# Revit family: Hager-WITTY PRO WALL MOUNTED-fr-FR-FR
name_source: partatom
category: Electrical Fixtures
units: mm (PartAtom-declared; Revit-internal decimal feet)

## family parameters
Always vertical = Yes
Cut with Voids When Loaded = No
Host = Wall
Maintain Annotation Orientation = No
OmniClass Number = 23.75.00.00
OmniClass Title = Climate Control (HVAC)
Part Type = Normal
Room Calculation Point = No
Round Connector Dimension = Use Diameter
Shared = No

## types (1)
- WITTY PRO-1x22kW-3P-XVL122SLM-WALL MOUNTED
    BC_METADATA = {"ObjectGuid":"b7395028-ef9e-46b8-b49f-e0fe9c8fa070","ModelGuid":"b1efb829-c177-4a88-8b0d-f632edc25d22","VariantGuid":"c7b0c534-fef0-4725-a2d6-e8a658ebdb92","Revision":"#2","VariantName":"REF 1"}
    BC_MODEL_ID = 1528908
    BC_OBJECT_ID = 511157
    BC_OBJECT_VERSION = #1
    BC_VARIANT_ID = 1164665
    Code hager = ADD_EC002883_ECVS_WO
    Default Elevation = 0 mm  [stored 0 ft]
    EF000003 - mode de pose = montage mural
    EF000008 - largeur = 250 mm  [stored 0.82021 ft]
    EF000040 - hauteur = 370 mm  [stored 1.21391 ft]
    EF000049 - profondeur = 150 mm  [stored 0.492126 ft]
    EF000458 - avec affichage = No
    EF001596 - matériau du boîtier/corps = plastique
    EF002136 - puissance de raccordement nominale = 22000 W
    EF003840 - tension d'entrée = 400 V
    EF004293 - indice de protection contre les chocs (IK) = IK10
    EF005455 - fréquence = 50/60 Hz
    EF005474 - indice de protection (IP) = IP55
    EF006577 - nombre de prises CEE = 0
    EF007001 - tension de sortie CC = 0 V
    EF007353 - courant de sortie max. CC = 0 A
    EF008200 - section de conducteur connectable = 0 m²
    EF009078 - nombre de points de chargement = 1
    EF009089 - avec boîte de raccordement domestique = No
    EF009091 - nombre d'interrupteurs différentiels type A = 0
    EF009092 - nombre d'interrupteurs différentiels type B = 0
    EF009300 - puissance max. par point de chargement = 22000 W
    EF009301 - nombre de coupleurs de charge type 1 = 0
    EF009302 - nombre de coupleurs de charge type 1 CCS = 0
    EF009303 - nombre de coupleurs de charge type 2 = 0
    EF009304 - nombre de coupleurs de charge type 2 CCS = 0
    EF009305 - nombre de prises de charge type 2 = 1
    EF009306 - nombre de coupleurs de charge GB CA = 0
    EF009307 - nombre de coupleurs de charge GB CC = 0
    EF009308 - nombre de prises de charge GB = 0
    EF009309 - nombre de prises de charge type 3 = 0
    EF009310 - nombre de coupleurs de charge CHAdeMO = 0
    EF009311 - nombre de prises de courant domestiques = 0
    EF009313 - avec compteur d'énergie = Yes
    EF009314 - avec disjoncteur de protection = No
    EF009547 - LTE = No
    EF011072 - compatible IFTTT = No
    EF012191 - avec lecteur de carte RFID intégré = Yes
    EF012361 - NFC (Near Field Communication) = No
    EF013154 - connectable via Wi-Fi = Yes
    EF014895 - longueur du câble de charge = 0 mm  [stored 0 ft]
    EF014925 - compatible avec Apple HomeKit = No
    EF014926 - compatible avec Google Assistant = No
    EF014927 - compatible avec Amazon Alexa = No
    EF016385 - standard radio 5G = No
    EF017508 - mise en réseau en maître = No
    EF017509 - détection de courant résiduel DC = No
    EF017511 - avec interrupteur à clé = No
    EF017512 - export de l'historique de charge = Yes
    EF017513 - version protocole OCPP (Open Charge Point Protocol) = 1.6
    EF017515 - Plug & Charge selon ISO 15118 = No
    EF017517 - mise en réseau comme extension = No
    EF017663 - câble de recharge avec verrouillage permanent sur la station de charge = No
    EF017664 - mise réseau via LAN = Yes
    EF017665 - compteur électrique compatible avec directive MID = Yes
    EF017668 - gestion intégrée de la charge statique = Yes
    EF017669 - convient pour une charge dynamique = Yes
    EF017672 - backend compris dans la livraison = No
    EF017972 - utilisation et configuration via application mobile = Yes
    EF025053 - exécution raccord côté installation = triphasé
    EFDE0066 - conforme à la législation sur l'étalonnage = No
    ETIM class code = EC002883
    ETIM class name = Charging device E-Mobility
    HG000003-Range = WITTY PRO
    HG000004-Manufacturer reference = XVL122SLM
    HG000065-With socket TE = No
    HG000099-Onfly Template ID = WittyOne_EVCS_Wall_Mounted
    Manufacturer = hager France
    Name = WITTY PRO WALL MOUNTED-FR
    Name BIM&CO = Electricity
    Name hager = ADD_ChargingStation_EC002883
    Reference = WITTY PRO-1x22kW-3P-XVL122SLM-WALL MOUNTED
    Reference description = ECVS Witty 1x22kW 3P T2S

note: [stored X ft] marks values corroborated as IEEE doubles in the binary element streams (Revit-internal decimal feet)
